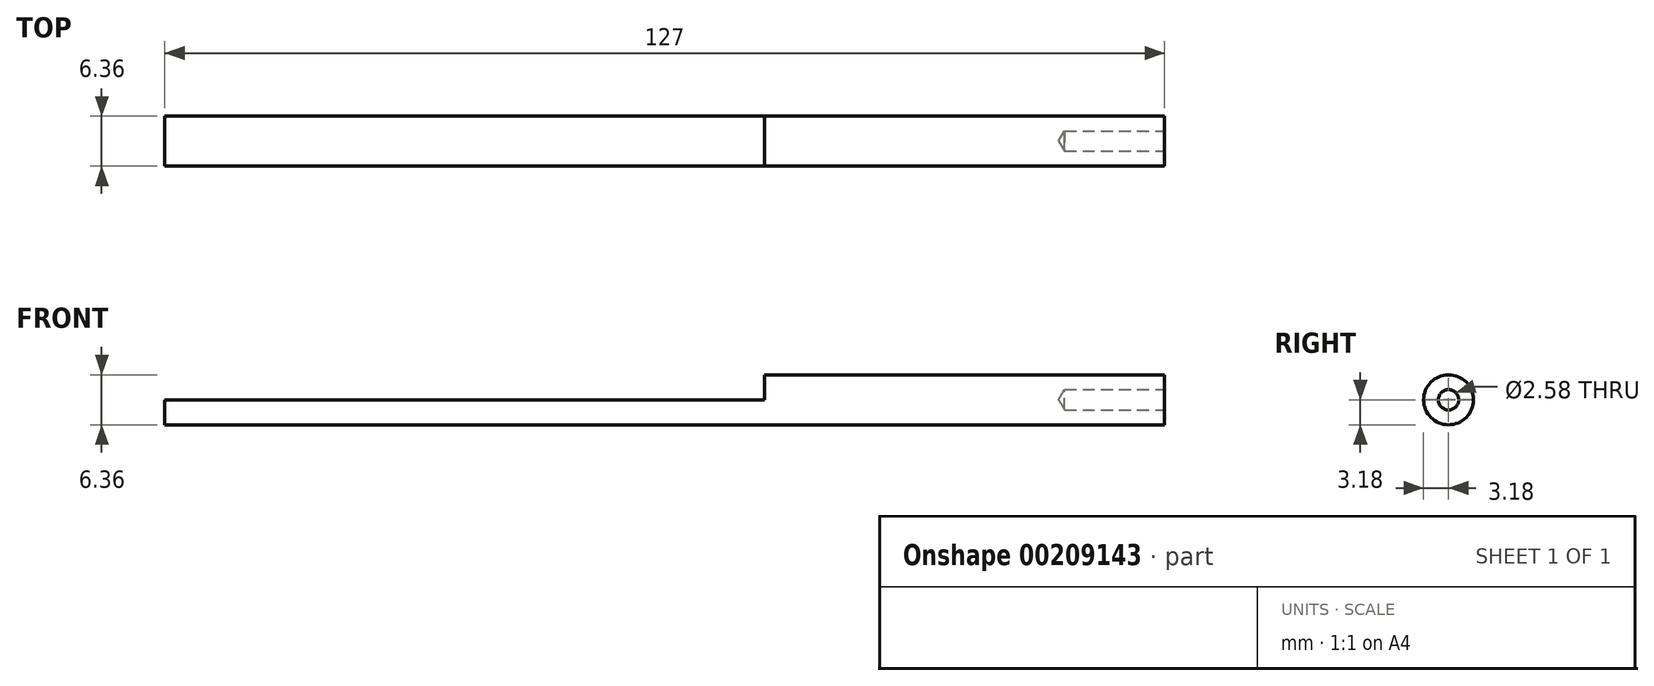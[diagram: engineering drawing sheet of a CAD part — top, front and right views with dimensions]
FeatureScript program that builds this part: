
annotation { "Feature Type Name" : "Feature", "Feature Type Description" : "" }
export const myFeature = defineFeature(function(context is Context, id is Id, definition is map)
    precondition{}
    {
        {
            var Q0;
            Q0=qCreatedBy(makeId("Right.planeOp"),FACE);
            var sketch = newSketch(context, id + "F0", { "sketchPlane" : qUnion([Q0])});
            skCircle(sketch, "E0", {"center": v(0, 0) * mm, "radius": 3.18 * mm});
            skSolve(sketch);
        }
        {
            var Q0;
            Q0=makeQuery(id+"F0.imprint","IMPRINT",FACE,{"disambiguationData":[TD([[makeQuery(id+"F0.imprint","IMPRINT",EDGE,{"derivedFrom":sQuery(id+"F0.wireOp",EDGE,"E0")}),1.0]])]});
            extrude(context, id + "F1", {"entities" : qUnion([Q0]), "depth" : 127 * mm});
        }
        {
            var Q0;
            Q0=makeQuery(id+"F1.opExtrude","CAP_FACE",FACE,{"disambiguationData":[OSD([sQuery(id+"F0.wireOp",EDGE,"E0")])],"isStart":false});
            var sketch = newSketch(context, id + "F2", { "sketchPlane" : qUnion([Q0])});
            skPoint(sketch, "E1", {"position": v(0, 0) * mm});
            skSolve(sketch);
        }
        {
            var Q0;
            Q0=sQuery(id+"F2.wireOp",VERTEX,"E1");
            var Q1;
            Q1=makeQuery(id+"F1.opExtrude","SWEPT_BODY",BODY,{"disambiguationData":[OSD([sQuery(id+"F0.wireOp",EDGE,"E0")])]});
            hole(context, id + "F3", {"style" : HoleStyle.SIMPLE, "endStyle" : HoleEndStyle.BLIND, "standardTappedOrClearance" : lookupTablePath({ "standard" : "ANSI", "engagement" : "75%", "pitch" : "40 tpi", "size" : "#5", "type" : "Tapped" }), "standardBlindInLast" : lookupTablePath({ "standard" : "ANSI", "engagement" : "75%", "pitch" : "40 tpi", "size" : "#5", "type" : "Tapped" }), "holeDiameter" : 2.58 * mm, "holeDepth" : 12.7 * mm, "startFromSketch" : true, "locations" : qUnion([Q0]), "scope" : qUnion([Q1]), "majorDiameter" : 3.18 * mm});
        }
        {
            var Q0;
            Q0=makeQuery(id+"F1.opExtrude","CAP_FACE",FACE,{"disambiguationData":[OSD([sQuery(id+"F0.wireOp",EDGE,"E0")])],"isStart":true});
            var sketch = newSketch(context, id + "F4", { "sketchPlane" : qUnion([Q0])});
            skCircle(sketch, "E2", {"center": v(0, 0) * mm, "radius": 0.83 * mm});
            skLineSegment(sketch, "E3", {"start": v(-3.18, 0) * mm, "end": v(-0.83, 0) * mm});
            skLineSegment(sketch, "E4", {"start": v(-0.83, 0) * mm, "end": v(0.83, 0) * mm});
            skLineSegment(sketch, "E5", {"start": v(0.83, 0) * mm, "end": v(3.18, 0) * mm});
            skSolve(sketch);
        }
        {
            var Q0;
            {var subQ1=sQuery(id+"F4.wireOp",EDGE,"E3");Q0=makeQuery(id+"F4.imprint","IMPRINT",FACE,{"disambiguationData":[TD([[makeQuery(id+"F4.imprint","IMPRINT",EDGE,{"derivedFrom":subQ1}),1.0]])]});}
            var Q1;
            {var subQ0=sQuery(id+"F4.wireOp",EDGE,"E4");Q1=makeQuery(id+"F4.imprint","IMPRINT",FACE,{"disambiguationData":[TD([[makeQuery(id+"F4.imprint","IMPRINT",EDGE,{"derivedFrom":subQ0}),1.0]])]});}
            extrude(context, id + "F5", {"entities" : qUnion([Q0, Q1]), "operationType" : NewBodyOperationType.REMOVE, "oppositeDirection" : true, "depth" : 76.2 * mm});
        }
    });
